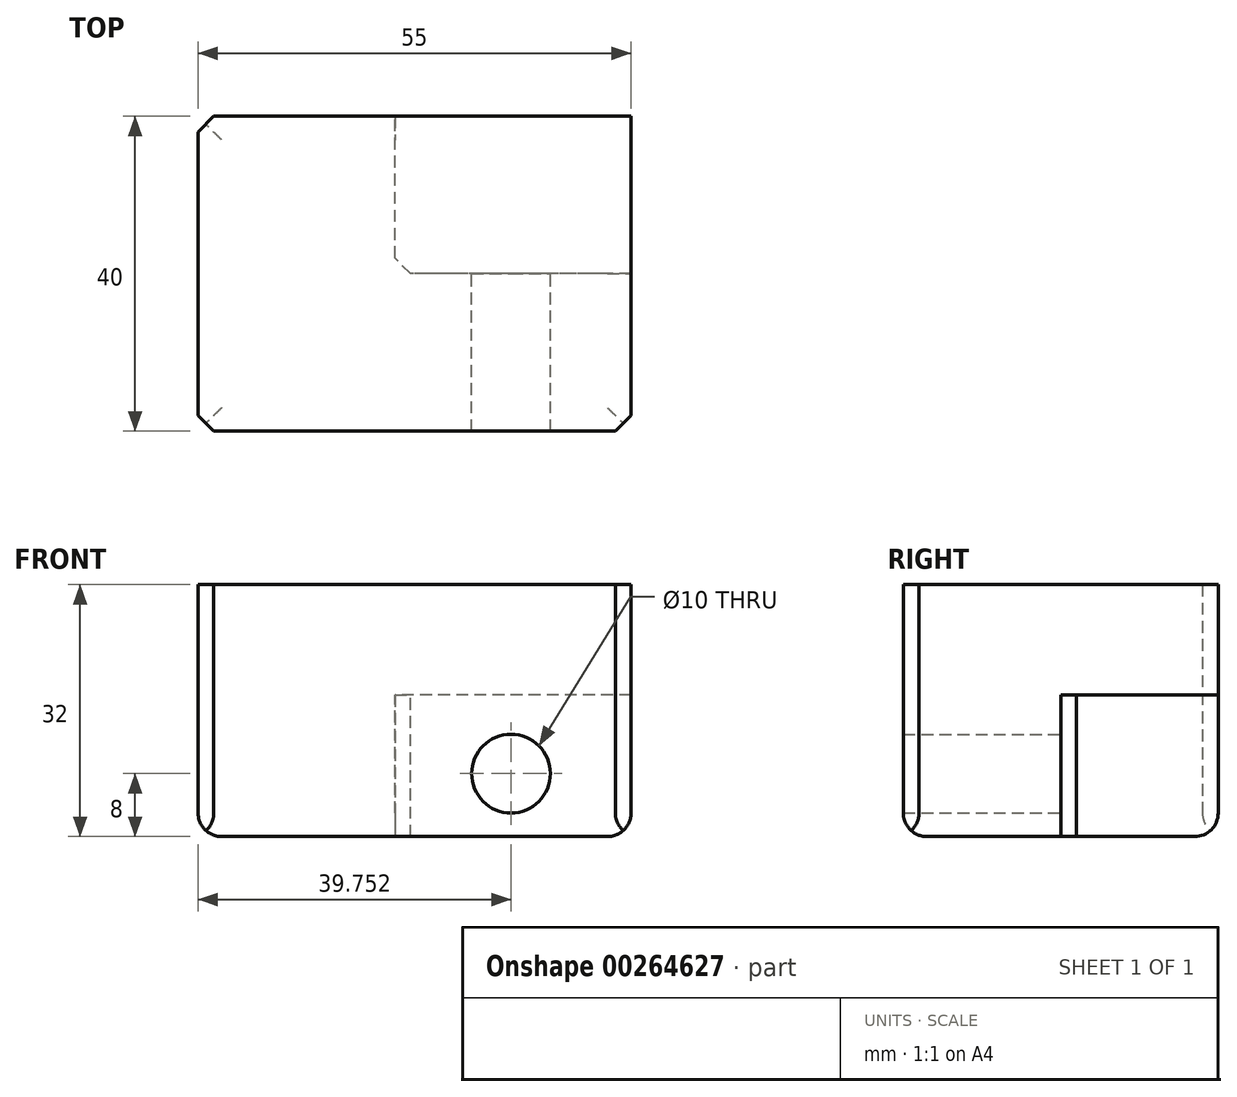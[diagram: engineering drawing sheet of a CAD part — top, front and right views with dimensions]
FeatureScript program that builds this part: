
annotation { "Feature Type Name" : "Feature", "Feature Type Description" : "" }
export const myFeature = defineFeature(function(context is Context, id is Id, definition is map)
    precondition{}
    {
        {
            var Q0;
            Q0=qCreatedBy(makeId("Front.planeOp"),FACE);
            var sketch = newSketch(context, id + "F0", { "sketchPlane" : qUnion([Q0])});
            skLineSegment(sketch, "E0.bottom", {"start": v(0, 0) * mm, "end": v(55, 0) * mm});
            skLineSegment(sketch, "E0.top", {"start": v(0, -32) * mm, "end": v(55, -32) * mm});
            skLineSegment(sketch, "E0.left", {"start": v(0, 0) * mm, "end": v(0, -32) * mm});
            skLineSegment(sketch, "E0.right", {"start": v(55, 0) * mm, "end": v(55, -32) * mm});
            skSolve(sketch);
        }
        {
            var Q0;
            Q0 = qSketchRegion(id + "F0", true);
            extrude(context, id + "F1", {"entities" : qUnion([Q0]), "depth" : 40 * mm});
        }
        {
            var Q0;
            Q0=qCreatedBy(makeId("Front.planeOp"),FACE);
            var sketch = newSketch(context, id + "F2", { "sketchPlane" : qUnion([Q0])});
            skLineSegment(sketch, "E1.bottom", {"start": v(55, -32) * mm, "end": v(25, -32) * mm});
            skLineSegment(sketch, "E1.top", {"start": v(55, -14) * mm, "end": v(25, -14) * mm});
            skLineSegment(sketch, "E1.left", {"start": v(55, -32) * mm, "end": v(55, -14) * mm});
            skLineSegment(sketch, "E1.right", {"start": v(25, -32) * mm, "end": v(25, -14) * mm});
            skSolve(sketch);
        }
        {
            var Q0;
            Q0=makeQuery(id+"F2.imprint","IMPRINT",FACE,{"disambiguationData":[TD([[makeQuery(id+"F2.imprint","IMPRINT",EDGE,{"derivedFrom":sQuery(id+"F2.wireOp",EDGE,"E1.bottom")}),-1.0]])]});
            extrude(context, id + "F3", {"entities" : qUnion([Q0]), "operationType" : NewBodyOperationType.REMOVE, "depth" : 20 * mm});
        }
        {
            var Q0;
            Q0=makeQuery(id+"F3.boolean.opBoolean","COPY",FACE,{"derivedFrom":makeQuery(id+"F3.opExtrude","CAP_FACE",FACE,{"disambiguationData":[OSD([sQuery(id+"F2.wireOp",EDGE,"E1.bottom"),sQuery(id+"F2.wireOp",EDGE,"E1.top"),sQuery(id+"F2.wireOp",EDGE,"E1.left"),sQuery(id+"F2.wireOp",EDGE,"E1.right")])],"isStart":false})});
            var sketch = newSketch(context, id + "F4", { "sketchPlane" : qUnion([Q0])});
            skCircle(sketch, "E2", {"center": v(-39.75, -24) * mm, "radius": 5 * mm});
            skSolve(sketch);
        }
        {
            var Q0;
            Q0=makeQuery(id+"F4.imprint","IMPRINT",FACE,{"disambiguationData":[TD([[makeQuery(id+"F4.imprint","IMPRINT",EDGE,{"derivedFrom":sQuery(id+"F4.wireOp",EDGE,"E2")}),1.0]])]});
            extrude(context, id + "F5", {"entities" : qUnion([Q0]), "operationType" : NewBodyOperationType.REMOVE, "endBound" : BoundingType.THROUGH_ALL, "oppositeDirection" : true, "depth" : 25 * mm});
        }
        {
            var Q0;
            Q0=makeQuery(id+"F1.opExtrude","CAP_EDGE",EDGE,{"disambiguationData":[OSD([sQuery(id+"F0.wireOp",EDGE,"E0.left")])],"isStart":true});
            var Q1;
            Q1=makeQuery(id+"F3.boolean.opBoolean","COPY",EDGE,{"derivedFrom":makeQuery(id+"F3.opExtrude","SWEPT_EDGE",EDGE,{"disambiguationData":[OSD([sQuery(id+"F2.wireOp",EDGE,"E1.bottom"),sQuery(id+"F2.wireOp",EDGE,"E1.right")])]})});
            var Q2;
            Q2=makeQuery(id+"F3.boolean.opBoolean","COPY",EDGE,{"derivedFrom":makeQuery(id+"F3.opExtrude","CAP_EDGE",EDGE,{"disambiguationData":[OSD([sQuery(id+"F2.wireOp",EDGE,"E1.right")])],"isStart":true})});
            var Q3;
            Q3=makeQuery(id+"F3.boolean.opBoolean","COPY",EDGE,{"derivedFrom":makeQuery(id+"F3.opExtrude","CAP_EDGE",EDGE,{"disambiguationData":[OSD([sQuery(id+"F2.wireOp",EDGE,"E1.left")])],"isStart":false})});
            var Q4;
            Q4=makeQuery(id+"F3.boolean.opBoolean","COPY",EDGE,{"derivedFrom":makeQuery(id+"F3.opExtrude","CAP_EDGE",EDGE,{"disambiguationData":[OSD([sQuery(id+"F2.wireOp",EDGE,"E1.right")])],"isStart":false})});
            var Q5;
            Q5=makeQuery(id+"F1.opExtrude","CAP_EDGE",EDGE,{"disambiguationData":[OSD([sQuery(id+"F0.wireOp",EDGE,"E0.right")])],"isStart":false});
            var Q6;
            Q6=makeQuery(id+"F1.opExtrude","CAP_EDGE",EDGE,{"disambiguationData":[OSD([sQuery(id+"F0.wireOp",EDGE,"E0.left")])],"isStart":false});
            chamfer(context, id + "F6", {"entities" : qUnion([Q0, Q1, Q2, Q3, Q4, Q5, Q6]), "width" : 2 * mm, "tangentPropagation" : true});
        }
        {
            var Q0;
            Q0=makeQuery(id+"F6.opChamfer","BLEND_EDGE",EDGE,{"blendedFrom":[makeQuery(id+"F3.boolean.opBoolean","COPY",EDGE,{"derivedFrom":makeQuery(id+"F3.opExtrude","SWEPT_EDGE",EDGE,{"disambiguationData":[OSD([sQuery(id+"F2.wireOp",EDGE,"E1.bottom"),sQuery(id+"F2.wireOp",EDGE,"E1.right")])]})}),makeQuery(id+"F1.opExtrude","SWEPT_FACE",FACE,{"disambiguationData":[OSD([sQuery(id+"F0.wireOp",EDGE,"E0.top")])]})],"blendedInto":[makeQuery(id+"F1.opExtrude","SWEPT_FACE",FACE,{"disambiguationData":[OSD([sQuery(id+"F0.wireOp",EDGE,"E0.top")])]})]});
            var Q1;
            Q1=makeQuery(id+"F6.opChamfer","BLEND_EDGE",EDGE,{"blendedFrom":[makeQuery(id+"F3.boolean.opBoolean","COPY",VERTEX,{"derivedFrom":makeQuery(id+"F3.opExtrude","CAP_VERTEX",VERTEX,{"disambiguationData":[OSD([sQuery(id+"F2.wireOp",EDGE,"E1.bottom"),sQuery(id+"F2.wireOp",EDGE,"E1.right")])],"isStart":false})}),makeQuery(id+"F1.opExtrude","SWEPT_FACE",FACE,{"disambiguationData":[OSD([sQuery(id+"F0.wireOp",EDGE,"E0.top")])]})],"blendedInto":[makeQuery(id+"F1.opExtrude","SWEPT_FACE",FACE,{"disambiguationData":[OSD([sQuery(id+"F0.wireOp",EDGE,"E0.top")])]})]});
            var Q2;
            Q2=makeQuery(id+"F6.opChamfer","BLEND_EDGE",EDGE,{"blendedFrom":[makeQuery(id+"F3.boolean.opBoolean","COPY",EDGE,{"derivedFrom":makeQuery(id+"F3.opExtrude","CAP_EDGE",EDGE,{"disambiguationData":[OSD([sQuery(id+"F2.wireOp",EDGE,"E1.bottom")])],"isStart":false})}),makeQuery(id+"F1.opExtrude","SWEPT_FACE",FACE,{"disambiguationData":[OSD([sQuery(id+"F0.wireOp",EDGE,"E0.top")])]})],"blendedInto":[makeQuery(id+"F1.opExtrude","SWEPT_FACE",FACE,{"disambiguationData":[OSD([sQuery(id+"F0.wireOp",EDGE,"E0.top")])]})]});
            var Q3;
            Q3=makeQuery(id+"F1.opExtrude","SWEPT_EDGE",EDGE,{"disambiguationData":[OSD([sQuery(id+"F0.wireOp",EDGE,"E0.top"),sQuery(id+"F0.wireOp",EDGE,"E0.right")])]});
            var Q4;
            Q4=makeQuery(id+"F1.opExtrude","CAP_EDGE",EDGE,{"disambiguationData":[OSD([sQuery(id+"F0.wireOp",EDGE,"E0.top")])],"isStart":false});
            var Q5;
            Q5=makeQuery(id+"F1.opExtrude","SWEPT_EDGE",EDGE,{"disambiguationData":[OSD([sQuery(id+"F0.wireOp",EDGE,"E0.top"),sQuery(id+"F0.wireOp",EDGE,"E0.left")])]});
            var Q6;
            Q6=makeQuery(id+"F1.opExtrude","CAP_EDGE",EDGE,{"disambiguationData":[OSD([sQuery(id+"F0.wireOp",EDGE,"E0.top")])],"isStart":true});
            fillet(context, id + "F7", {"entities" : qUnion([Q0, Q1, Q2, Q3, Q4, Q5, Q6]), "radius" : 3 * mm, "tangentPropagation" : true, "allowEdgeOverflow" : false});
        }
    });
